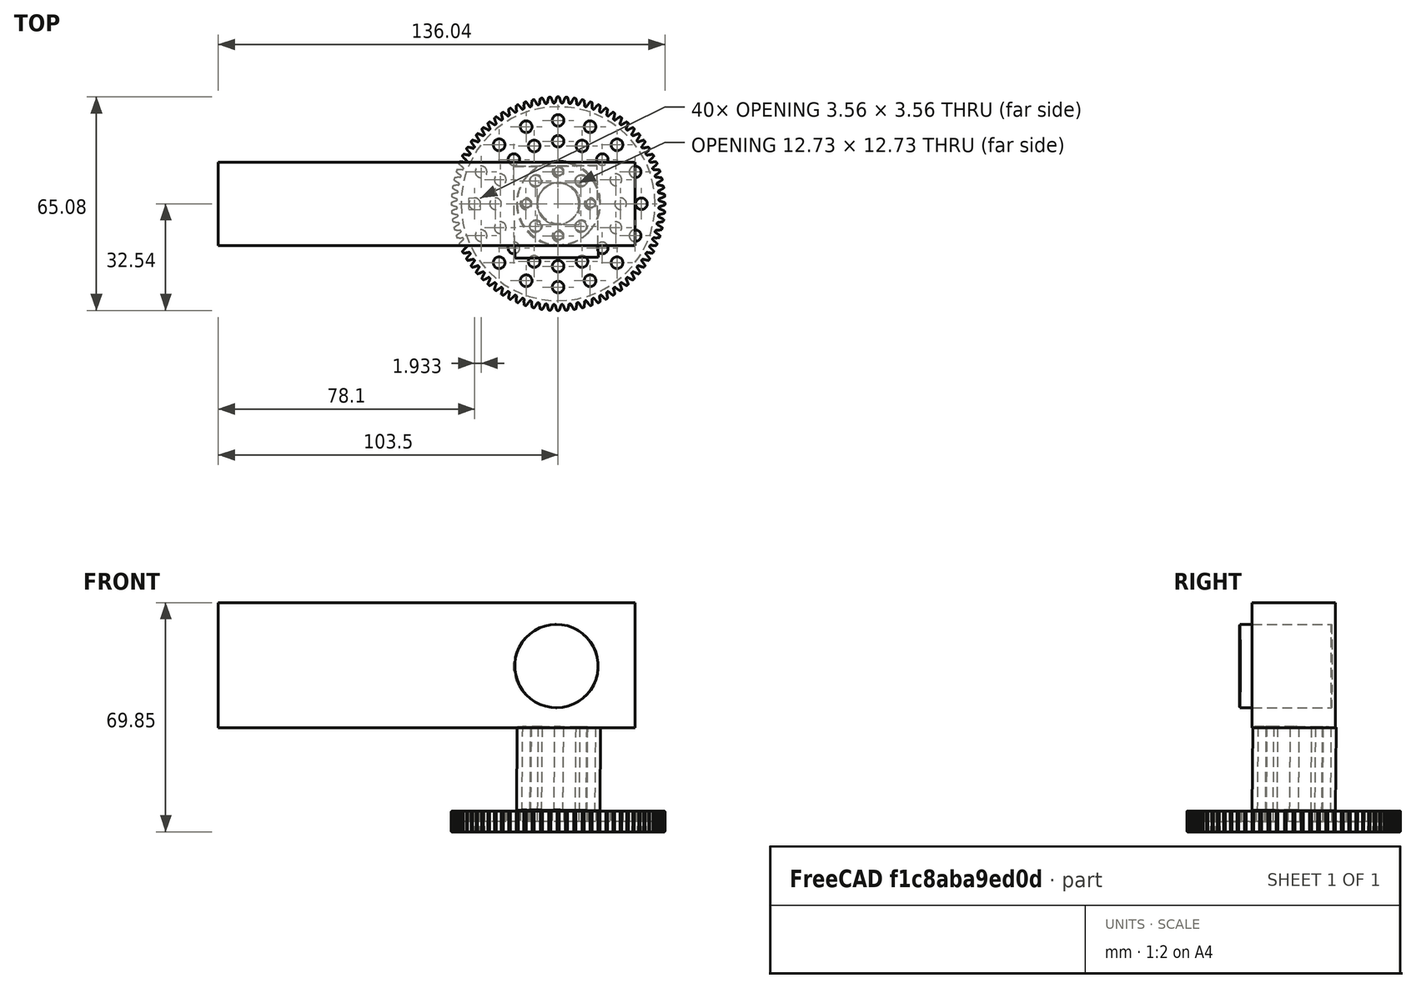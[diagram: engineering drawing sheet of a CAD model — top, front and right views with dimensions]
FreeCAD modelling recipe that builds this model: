
FCSTD DOCUMENT  (FreeCAD 0.15R4671 (Git))
Label: shoulder
License: All rights reserved
LicenseURL: http://en.wikipedia.org/wiki/All_rights_reserved
objects: Part::Feature×2, Part::Box×1, Part::Cylinder×1
note: 4 computed .brp shape members not serialized (recipe doc carries the construction recipe); baked Part::Feature solids carry a one-line shape summary decoded from their .brp

FEATURE [Part::Feature] Part__Feature  label="615206"
  Placement = pos=(0,0,3.175) rot=(0,-1,0;1.5708rad)
  shape: bbox 65.09 x 65.09 x 6.35 mm, 760 faces (baked)
FEATURE [Part::Feature] Part__Feature001  label="545386"
  Placement = pos=(0.0263083,-5.32278e-06,6.532) rot=(-0.730992,0.68238,-0.002886;0.01157rad)
  shape: bbox 25.59 x 25.61 x 25.69 mm, 22 faces (baked)
FEATURE [Part::Box] Box  label="Cube"
  Height = 38.1
  Length = 127
  Placement = pos=(-103.505,-12.7,31.75) rot=(0,0,1;0rad)
  Width = 25.4
FEATURE [Part::Cylinder] Cylinder
  Angle = 360
  Height = 27.94
  Placement = pos=(-0.483033,-16.4367,50.513) rot=(0.582648,-0.571473,-0.577876;4.18705rad)
  Radius = 12.7
